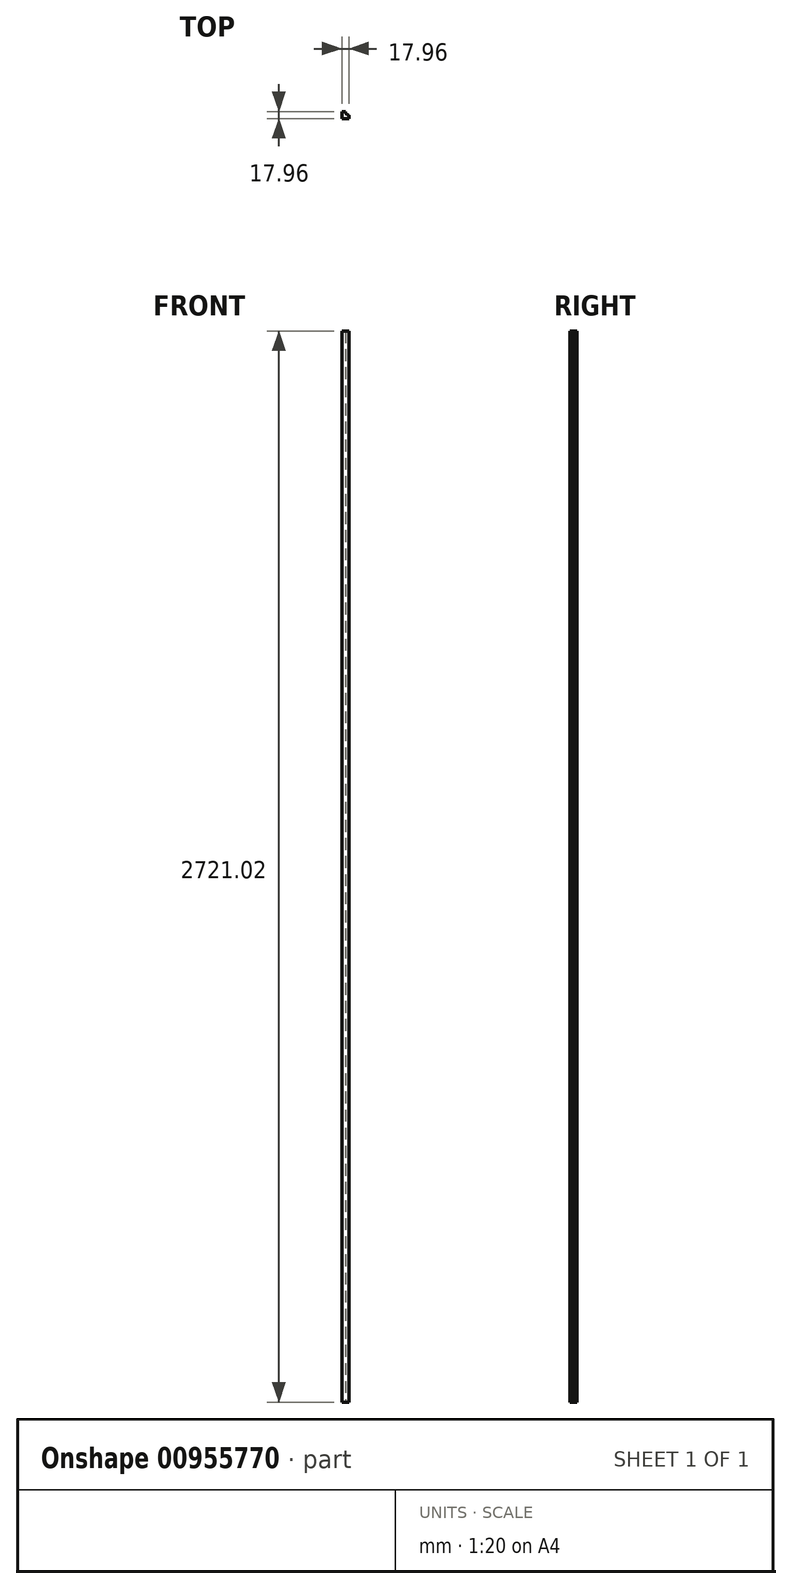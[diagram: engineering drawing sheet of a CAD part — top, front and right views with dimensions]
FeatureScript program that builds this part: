
annotation { "Feature Type Name" : "Feature", "Feature Type Description" : "" }
export const myFeature = defineFeature(function(context is Context, id is Id, definition is map)
    precondition{}
    {
        {
            var Q0;
            Q0=qCreatedBy(makeId("Top.planeOp"),FACE);
            var sketch = newSketch(context, id + "F0", { "sketchPlane" : qUnion([Q0])});
            skLineSegment(sketch, "E0.bottom", {"start": v(2.43, -14.48) * mm, "end": v(-15.53, -14.48) * mm});
            skLineSegment(sketch, "E0.top", {"start": v(2.43, -32.44) * mm, "end": v(-15.53, -32.44) * mm});
            skLineSegment(sketch, "E0.left", {"start": v(2.43, -14.48) * mm, "end": v(2.43, -32.44) * mm});
            skLineSegment(sketch, "E0.right", {"start": v(-15.53, -14.48) * mm, "end": v(-15.53, -32.44) * mm});
            skPoint(sketch, "E0.middle", {"position": v(-6.55, -23.46) * mm});
            skLineSegment(sketch, "E1", {"start": v(-6.55, -23.46) * mm, "end": v(2.43, -23.46) * mm});
            skCircle(sketch, "E2", {"center": v(2.43, -14.48) * mm, "radius": 8.98 * mm});
            skSolve(sketch);
        }
        {
            var Q0;
            {var subQ2=sQuery(id+"F0.wireOp",EDGE,"E0.top");Q0=makeQuery(id+"F0.imprint","IMPRINT",FACE,{"disambiguationData":[TD([[makeQuery(id+"F0.imprint","IMPRINT",EDGE,{"derivedFrom":subQ2}),-1.0]])]});}
            extrude(context, id + "F1", {"entities" : qUnion([Q0]), "depth" : 2721.02 * mm, "offsetDistance" : 25.4 * mm});
        }
    });
